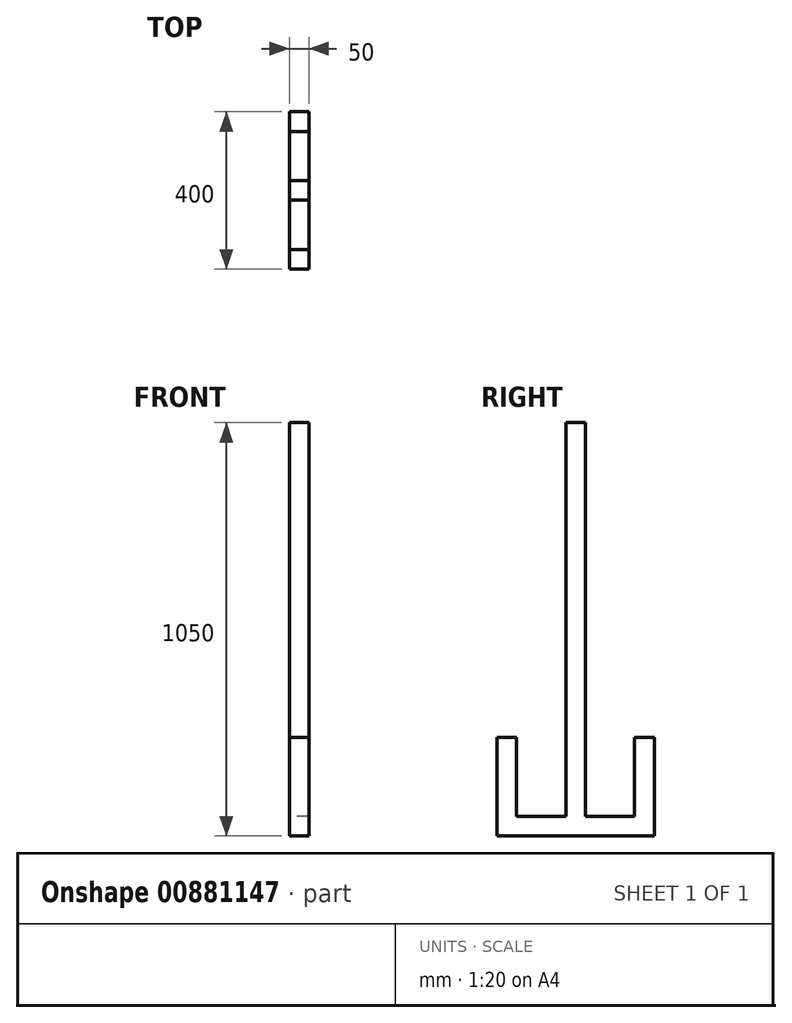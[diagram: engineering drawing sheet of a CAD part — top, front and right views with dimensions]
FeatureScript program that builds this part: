
annotation { "Feature Type Name" : "Feature", "Feature Type Description" : "" }
export const myFeature = defineFeature(function(context is Context, id is Id, definition is map)
    precondition{}
    {
        {
            var Q0;
            Q0=qCreatedBy(makeId("Top.planeOp"),FACE);
            var sketch = newSketch(context, id + "F0", { "sketchPlane" : qUnion([Q0])});
            skLineSegment(sketch, "E0.bottom", {"start": v(-25, 25) * mm, "end": v(25, 25) * mm});
            skLineSegment(sketch, "E0.top", {"start": v(-25, -25) * mm, "end": v(25, -25) * mm});
            skLineSegment(sketch, "E0.left", {"start": v(-25, 25) * mm, "end": v(-25, -25) * mm});
            skLineSegment(sketch, "E0.right", {"start": v(25, 25) * mm, "end": v(25, -25) * mm});
            skPoint(sketch, "E0.middle", {"position": v(0, 0) * mm});
            skSolve(sketch);
        }
        {
            var Q0;
            Q0=makeQuery(id+"F0.imprint","IMPRINT",FACE,{"disambiguationData":[TD([[makeQuery(id+"F0.imprint","IMPRINT",EDGE,{"derivedFrom":sQuery(id+"F0.wireOp",EDGE,"E0.bottom")}),-1.0]])]});
            extrude(context, id + "F1", {"entities" : qUnion([Q0]), "depth" : 1000 * mm, "offsetDistance" : 25 * mm});
        }
        {
            var Q0;
            Q0=qCreatedBy(makeId("Right.planeOp"),FACE);
            var sketch = newSketch(context, id + "F2", { "sketchPlane" : qUnion([Q0])});
            skPoint(sketch, "E1.middle", {"position": v(0, 0) * mm});
            skLineSegment(sketch, "E2.bottom", {"start": v(0, 0) * mm, "end": v(-200, 0) * mm});
            skLineSegment(sketch, "E2.top", {"start": v(0, -50) * mm, "end": v(-200, -50) * mm});
            skLineSegment(sketch, "E2.left", {"start": v(0, 0) * mm, "end": v(0, -50) * mm});
            skLineSegment(sketch, "E2.right", {"start": v(-200, 0) * mm, "end": v(-200, -50) * mm});
            skLineSegment(sketch, "E3.MirrorCS", {"start": v(0, 0) * mm, "end": v(200, 0) * mm});
            skLineSegment(sketch, "E4.MirrorCS", {"start": v(200, 0) * mm, "end": v(200, -50) * mm});
            skLineSegment(sketch, "E5.MirrorCS", {"start": v(0, -50) * mm, "end": v(200, -50) * mm});
            skSolve(sketch);
        }
        {
            var Q0;
            Q0 = qSketchRegion(id + "F2", true);
            extrude(context, id + "F3", {"entities" : qUnion([Q0]), "operationType" : NewBodyOperationType.ADD, "depth" : 25 * mm, "offsetDistance" : 25 * mm, "hasSecondDirection" : true, "secondDirectionOppositeDirection" : true, "secondDirectionDepth" : 25 * mm});
        }
        {
            var Q0;
            Q0=qCreatedBy(makeId("Right.planeOp"),FACE);
            var sketch = newSketch(context, id + "F4", { "sketchPlane" : qUnion([Q0])});
            skLineSegment(sketch, "E6.bottom", {"start": v(200, 0) * mm, "end": v(150, 0) * mm});
            skLineSegment(sketch, "E6.top", {"start": v(200, 200) * mm, "end": v(150, 200) * mm});
            skLineSegment(sketch, "E6.left", {"start": v(200, 0) * mm, "end": v(200, 200) * mm});
            skLineSegment(sketch, "E6.right", {"start": v(150, 0) * mm, "end": v(150, 200) * mm});
            skLineSegment(sketch, "E7", {"start": v(0, 0) * mm, "end": v(-200, 0) * mm, "construction": true});
            skLineSegment(sketch, "E8.bottom", {"start": v(-200, 0) * mm, "end": v(-150, 0) * mm});
            skLineSegment(sketch, "E8.top", {"start": v(-200, 200) * mm, "end": v(-150, 200) * mm});
            skLineSegment(sketch, "E8.left", {"start": v(-200, 0) * mm, "end": v(-200, 200) * mm});
            skLineSegment(sketch, "E8.right", {"start": v(-150, 0) * mm, "end": v(-150, 200) * mm});
            skSolve(sketch);
        }
        {
            var Q0;
            Q0 = qSketchRegion(id + "F4", true);
            extrude(context, id + "F5", {"entities" : qUnion([Q0]), "operationType" : NewBodyOperationType.ADD, "depth" : 25 * mm, "offsetDistance" : 25 * mm, "hasSecondDirection" : true, "secondDirectionOppositeDirection" : true, "secondDirectionDepth" : 25 * mm});
        }
    });
